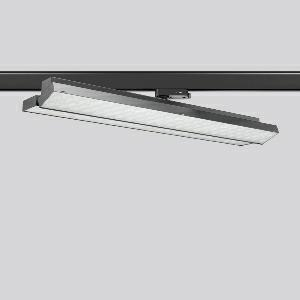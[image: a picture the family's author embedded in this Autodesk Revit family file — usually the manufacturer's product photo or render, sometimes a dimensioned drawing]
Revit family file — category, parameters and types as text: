
# Revit family: tx-move_742162_003_2_b54b
name_source: partatom
category: Lighting Fixtures
units: mm (PartAtom-declared; Revit-internal decimal feet)

## family parameters
Cut with Voids When Loaded = No
Host = Face
Light Source = No
Part Type = Normal
Room Calculation Point = No
Round Connector Dimension = Use Diameter
Shared = No

## types (1)
- MultiLumen 1 (1 x LED Modul 927, 2150 lm, 2700)
    Apparent Load = 38 VA
    CIE Flux Codes = 77 96 99 100 100
    Color Rendering = 92
    Color Temperature = 2700
    Default Elevation = 1800 mm
    Description = Series: TX-MOVE
Multifunctional surface-mounted spotlight for area lighting. Very flat design. Housing: sheet steel, powder-coated. Rotation range: 356°. Swivel range: 90°. Consistent alignment possible with visible tilt scale. High-efficiency LED units with optimum light control thanks to clear plastic (PC) lens optics. Spezielle Mikrostrukturen reduzieren Gelbsaum. Symmetrical light distribution. Best colour rendering with CRI >90 for fresh products and coloured textiles. With multi adaptor for 3-circuit tracks 230 V. Suitable for Track on ceiling. MultiLumen: Luminous flux adjustable in 3 steps. Factory setting is the highest luminous flux. Environmentally friendly and resource-saving due to replaceable and recyclable components. 
Colour: deep black, matt (RAL 9005)
Length: 570 mm
Width: 119 mm
Height: 92 mm
Lamp: LED
Socket: without socket
Colour temperature: 2700K
Colour rendering index (CRI): 90
System power: 38 W
Rated luminous flux: 4300 lm
Luminous efficiency: 113 lm/W
System power 2: 51 W
Rated luminous flux 2: 5600 lm
Luminous efficiency 2: 110 lm/W
System power 3: 62 W
Rated luminous flux 3: 6650 lm
Luminous efficiency 3: 107 lm/W
Control gear: Regulated power supply
Protection class: I
Type of protection: IP 20
    Height = 75 mm
    Lamp = 1 x LED Modul 927
    Lamp Light Flux = 2150 lm
    Lamp count = 1
    Length = 569 mm
    Lifetime = 50000 h
    Luminous efficacy = 113 lm/W
    Manufacturer = RZB
    ModVariant = No
    Model = 742162.003.2
    Mounting Place = Ceiling
    Mounting Type = Surface mounted
    Number of Poles = 1
    OnlyDefault = Yes
    Power Factor = 1
    Product Name = TX-MOVE
    Product group = Track mounted projectors
    ProductGroupID = 301
    Protection Class = Protection class I
    Protection Degree = IP 20
    RLX_Detail_Level = 1
    RLX_Emergency_Light_Flux = 0 lm
    RLX_Emergency_Type = 0
    RLX_Emergency_Type_DB = No
    RlxData = <blob elided: 36705 chars, md5=e9dbfa3f>
    Socket = socket
    Standby Power = 0 W
    System Light Flux = 4300 lm
    System Power = 38 W
    Type Comments = MultiLumen 1
    Type Image = 742162.003.jpg
    URL = http://relux.com
    VarID = multilumen_1
    Voltage = 0 V
    Weight = 0.00 kg
    Width = 119 mm

## geometry (parser evidence)
native form markers: Blend x4, Sweep x16
no freeform markers — native parametric forms only
